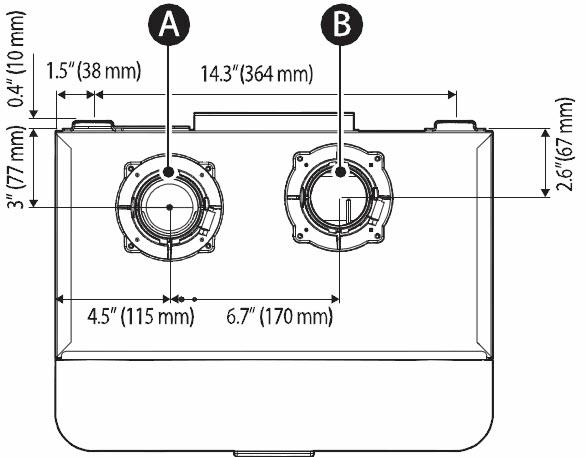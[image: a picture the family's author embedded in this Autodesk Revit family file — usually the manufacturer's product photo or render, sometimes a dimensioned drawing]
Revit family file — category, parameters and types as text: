
# Revit family: Water_Heater-Racks-Navien-NPE-3_Unit_Front---
name_source: partatom
category: Mechanical Equipment
revit_build: Autodesk Revit 2016 (Build: 20150220_1215(x64)
units: mm (PartAtom-declared; Revit-internal decimal feet)

## family parameters
Cut with Voids When Loaded = No
Host = Face
OmniClass Number = 23.65.35.11
OmniClass Title = Supply Water Heaters
Part Type = Normal
Room Calculation Point = No
Round Connector Dimension = Use Diameter
Shared = No

## types (4) — shared parameters
2" Exhaust/Intake = Yes
3" Exhaust/Intake = No
Apparent Load = 0 VA
Assembly Code = D3010500
Certifications = Energy Star | AHRI | CSA | CSA | NFS
Cold Water Inlet = 1"
Configuration = NPE_F3_3F
Default Elevation = 48 "
Depth = 23.8 "
Description = 3 Unit Front
Exhaust = 2"
Finish = Metal - Navien - White
Flow Rate = 1 GPM
Flow Rate Note = 35°F (19°C) temp rise: 11.2 GPM (42 L/m) | 45°F (25°C) temp rise: 8.7 GPM (33 L/m) | 67°F (36°C) temp rise: NPE-240A: 5.6 GPM(21 L/m), NPE-240S: 5.7 GPM(22 L/m)
Frequency = 60 Hz
Gas Inlet = 1"
Heating Capacity = 120000.0 Btu/h
Heating Capacity Note = 19,900–199,900 (BTU/H)
Height = 65.5 "
Hot Water Outlet = 1"
Ignition = Electronic ignition
Installation Type = Indoor
Intake = 2"
Keynote = 22 33 00.A1
Manifold(s) = (1) 30019041A
Manufacturer = Navien, Inc.
Manufacturer Fax Number = (949) 420-0430
Natural Gas Manifold Pressure = -0.05" WC to -0.58" WC
Natural Gas Supply Pressure = 3.5"–10.5" WC
Number of Poles = 1
Phase = 1
Power Factor = 1
Product Documentation Link = https://www.navieninc.com
Product Name = NPE Series Tankless Water Heaters w/ Racks
Product Page URL = https://www.navieninc.com
Propane Gas Manifold Pressure = -0.10" WC to -0.78" WC
Propane Gas Supply Pressure = 8"–13" WC
Rack(s) = (1) GFFM-KDIZUS-003 + (2) GFFM-KDIZUS-004
Required Cascade Operation Accessory = (3) 30014367A (Common Vent Damper & Cascade Communication Cable) or (2) GXXX000546 (Individual Vent Cascade Communication Cable)
Type Comments = For Wall Mount RL Manifold systems- Exclude Base & Add-on Racks
URL = https://www.navieninc.com
Venting = Exhaust: 2" PVC, CPVC, PP, SS / 2" special gas vent type BH (Class II, A/B/C) | Intake: 2" PVC, CPVC, PP, SS / 2" special gas vent type BH (Class II, A/B/C) | Vent clearances: 0" to combustibles
Venting Type = Forced draft direct vent
Version = 2016 - v1.0.a
Voltage = 120 V
Water Pressure = 15–150 PSI
Wi-Fi Ready = NaviLink Wi-Fi Control: PBCM-AS-001
Width = 62.3 "

## per-type parameters (varying)
| type | Constraints | Model | Natural Gas | Propane Gas | Recirculation Inlet | Recirculation Inlet Visibility | Tankless Water Heaters | Weight |
| Natural Gas - Recirculating System - NPE-240A(Advanced)-NG | 6 | (3) NPE-240A-NG | Yes | No | 0" | Yes | (3) NPE-240A-NG | 82.00 lbf |
| Natural Gas - NPE-240S(Standard)-NG | 7 | (3) NPE-240S-NG | Yes | No | 1" | No | (3) NPE-240S-NG | 75.00 lbf |
| Propane Gas - Recirculating System - NPE-240A(Advanced)-LPG | 6 | (3) NPE-240A-LPG | No | Yes | 0" | Yes | (3) NPE-240A-LPG | 82.00 lbf |
| Propane Gas - NPE-240S(Standard)-LPG | 7 | (3) NPE-240S-LPG | No | Yes | 1" | No | (3) NPE-240S-LPG | 75.00 lbf |

## geometry (parser evidence)
native form markers: Sweep x23
no freeform markers — native parametric forms only
